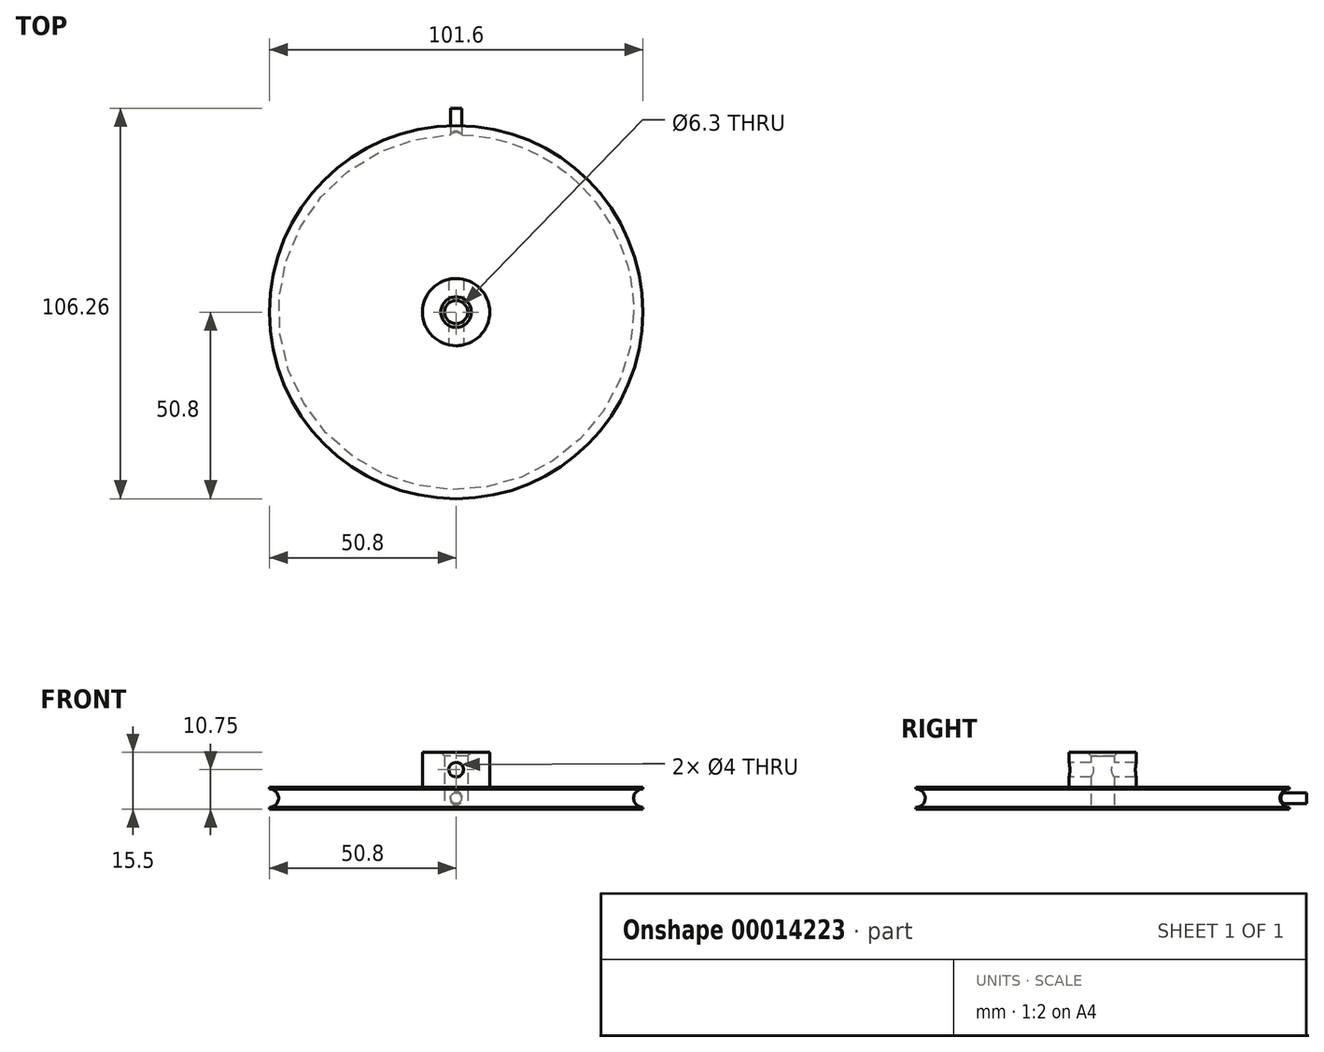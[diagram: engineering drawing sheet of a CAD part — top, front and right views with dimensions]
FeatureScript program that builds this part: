
annotation { "Feature Type Name" : "Feature", "Feature Type Description" : "" }
export const myFeature = defineFeature(function(context is Context, id is Id, definition is map)
    precondition{}
    {
        {
            var Q0;
            Q0=qCreatedBy(makeId("Top.planeOp"),FACE);
            var sketch = newSketch(context, id + "F0", { "sketchPlane" : qUnion([Q0])});
            skCircle(sketch, "E0", {"center": v(0, 0) * mm, "radius": 3.15 * mm});
            skCircle(sketch, "E1", {"center": v(0, 0) * mm, "radius": 9.15 * mm});
            skCircle(sketch, "E2", {"center": v(0, 0) * mm, "radius": 50.8 * mm});
            skSolve(sketch);
        }
        {
            var Q0;
            Q0=makeQuery(id+"F0.imprint","IMPRINT",FACE,{"disambiguationData":[TD([[makeQuery(id+"F0.imprint","IMPRINT",EDGE,{"derivedFrom":sQuery(id+"F0.wireOp",EDGE,"E0")}),-1.0]])]});
            extrude(context, id + "F1", {"entities" : qUnion([Q0]), "depth" : 15.5 * mm});
        }
        {
            var Q0;
            Q0=makeQuery(id+"F0.imprint","IMPRINT",FACE,{"disambiguationData":[TD([[makeQuery(id+"F0.imprint","IMPRINT",EDGE,{"derivedFrom":sQuery(id+"F0.wireOp",EDGE,"E1")}),-1.0]])]});
            extrude(context, id + "F2", {"entities" : qUnion([Q0]), "operationType" : NewBodyOperationType.ADD, "depth" : 6 * mm});
        }
        {
            var Q0;
            Q0=qCreatedBy(makeId("Front.planeOp"),FACE);
            var sketch = newSketch(context, id + "F3", { "sketchPlane" : qUnion([Q0])});
            skLineSegment(sketch, "E3", {"start": v(-50.8, 0) * mm, "end": v(-50.8, 6) * mm});
            skArc(sketch, "E4", {"start": v(-50.8, 0.5) * mm, "mid": v(-48.3, 3) * mm, "end": v(-50.8, 5.5) * mm});
            skLineSegment(sketch, "E5", {"start": v(-50.8, 3) * mm, "end": v(-48.3, 3) * mm, "construction": true});
            skLineSegment(sketch, "E6", {"start": v(-50.8, 5.5) * mm, "end": v(-50.03, 5.5) * mm, "construction": true});
            skLineSegment(sketch, "E7", {"start": v(-50.8, 0.5) * mm, "end": v(-50.8, 5.5) * mm});
            skSolve(sketch);
        }
        {
            var Q0;
            Q0 = qSketchRegion(id + "F3", true);
            var Q1;
            Q1=makeQuery(id+"F1.opExtrude","CAP_EDGE",EDGE,{"disambiguationData":[OSD([sQuery(id+"F0.wireOp",EDGE,"E0")])],"isStart":false});
            revolve(context, id + "F4", {"operationType" : NewBodyOperationType.REMOVE, "entities" : qUnion([Q0]), "axis" : qUnion([Q1]), "revolveType" : RevolveType.FULL, "oppositeDirection" : true});
        }
        {
            var Q0;
            Q0=qCreatedBy(makeId("Front.planeOp"),FACE);
            var sketch = newSketch(context, id + "F5", { "sketchPlane" : qUnion([Q0])});
            skLineSegment(sketch, "E8", {"start": v(-9.15, 5.97) * mm, "end": v(-9.15, 15.53) * mm});
            skLineSegment(sketch, "E9.0", {"start": v(-9.15, 15.5) * mm, "end": v(9.15, 15.5) * mm});
            skLineSegment(sketch, "E10", {"start": v(9.15, 15.5) * mm, "end": v(9.15, 5.97) * mm});
            skLineSegment(sketch, "E11.0", {"start": v(-50.8, 6) * mm, "end": v(50.8, 6) * mm});
            skLineSegment(sketch, "E12", {"start": v(0, 15.5) * mm, "end": v(0, 6) * mm, "construction": true});
            skLineSegment(sketch, "E13", {"start": v(-9.15, 15.53) * mm, "end": v(9.15, 5.97) * mm, "construction": true});
            skLineSegment(sketch, "E14", {"start": v(9.1, 15.5) * mm, "end": v(-9.15, 5.97) * mm, "construction": true});
            skCircle(sketch, "E15", {"center": v(0, 10.75) * mm, "radius": 2 * mm});
            skSolve(sketch);
        }
        {
            var Q0;
            Q0=makeQuery(id+"F5.imprint","IMPRINT",FACE,{"disambiguationData":[TD([[makeQuery(id+"F5.imprint","IMPRINT",EDGE,{"derivedFrom":sQuery(id+"F5.wireOp",EDGE,"E15")}),1.0]])]});
            extrude(context, id + "F6", {"entities" : qUnion([Q0]), "operationType" : NewBodyOperationType.REMOVE, "endBound" : BoundingType.THROUGH_ALL, "oppositeDirection" : true, "depth" : 25.4 * mm, "hasSecondDirection" : true, "secondDirectionBound" : SecondDirectionBoundingType.THROUGH_ALL, "secondDirectionOppositeDirection" : false, "secondDirectionDepth" : 25.4 * mm});
        }
        {
            var Q0;
            Q0=makeQuery(id+"F1.opExtrude","CAP_EDGE",EDGE,{"disambiguationData":[OSD([sQuery(id+"F0.wireOp",EDGE,"E0")])],"isStart":false});
            chamfer(context, id + "F7", {"entities" : qUnion([Q0]), "width" : 1 * mm, "tangentPropagation" : true});
        }
        {
            var Q0;
            Q0=qCreatedBy(makeId("Front.planeOp"),FACE);
            var sketch = newSketch(context, id + "F8", { "sketchPlane" : qUnion([Q0])});
            skLineSegment(sketch, "E16.0", {"start": v(-50.8, 6) * mm, "end": v(50.8, 6) * mm});
            skLineSegment(sketch, "E17.0", {"start": v(-50.8, 0) * mm, "end": v(50.8, 0) * mm});
            skLineSegment(sketch, "E18", {"start": v(-50.8, 6) * mm, "end": v(50.8, 0) * mm, "construction": true});
            skLineSegment(sketch, "E19", {"start": v(50.8, 6) * mm, "end": v(-50.8, 0) * mm, "construction": true});
            skCircle(sketch, "E20", {"center": v(0, 3) * mm, "radius": 1.5 * mm});
            skSolve(sketch);
        }
        {
            var Q0;
            Q0=makeQuery(id+"F8.imprint","IMPRINT",FACE,{"disambiguationData":[TD([[makeQuery(id+"F8.imprint","IMPRINT",EDGE,{"derivedFrom":sQuery(id+"F8.wireOp",EDGE,"E20")}),1.0]])]});
            extrude(context, id + "F9", {"entities" : qUnion([Q0]), "operationType" : NewBodyOperationType.ADD, "oppositeDirection" : true, "depth" : 55.46 * mm, "hasSecondDirection" : true, "secondDirectionOppositeDirection" : true, "secondDirectionDepth" : 25 * mm});
        }
        {
            var Q0;
            Q0=makeQuery(id+"F9.boolean.opBoolean","INTERSECT",EDGE,{"derivedFrom":[makeQuery(id+"F4.boolean.opBoolean","COPY",FACE,{"derivedFrom":makeQuery(id+"F4.opRevolve","SWEPT_FACE",FACE,{"disambiguationData":[OSD([sQuery(id+"F3.wireOp",EDGE,"E4")])]})}),makeQuery(id+"F9.opExtrude","SWEPT_FACE",FACE,{"disambiguationData":[OSD([sQuery(id+"F8.wireOp",EDGE,"E20")])]})]});
            fillet(context, id + "F10", {"entities" : qUnion([Q0]), "radius" : 0.2 * mm, "tangentPropagation" : true, "allowEdgeOverflow" : false});
        }
    });
